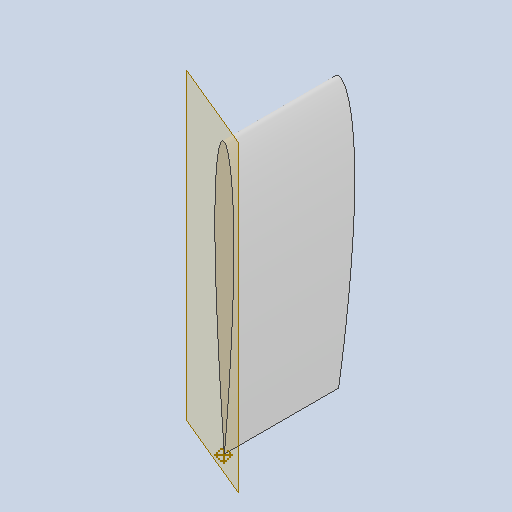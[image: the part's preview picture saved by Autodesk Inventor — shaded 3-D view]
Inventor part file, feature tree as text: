
AUTODESK INVENTOR PART (.ipt)
format: ipt  version: 2025.2 (Build 292293000, 293)  size: 198,144 bytes
history: native  units: in
note: dims shown in document units (in); Inventor stores cm internally (conversion verified against a paired STEP export)
features: other x4, plane x2
ambient origin geometry x8: Origin, YZ Plane, XZ Plane, XY Plane, X Axis, Y Axis, Z Axis, Center Point
bodies: Body1 (feature_tree)
feature tree (6):
  other  "Part1.ipt"
  plane  "Work Plane3"
  other  "Work Point1"
  other  "Solid2::Part1.ipt"
  other  "TaggingFeature1"
  plane  "Work Plane1"
